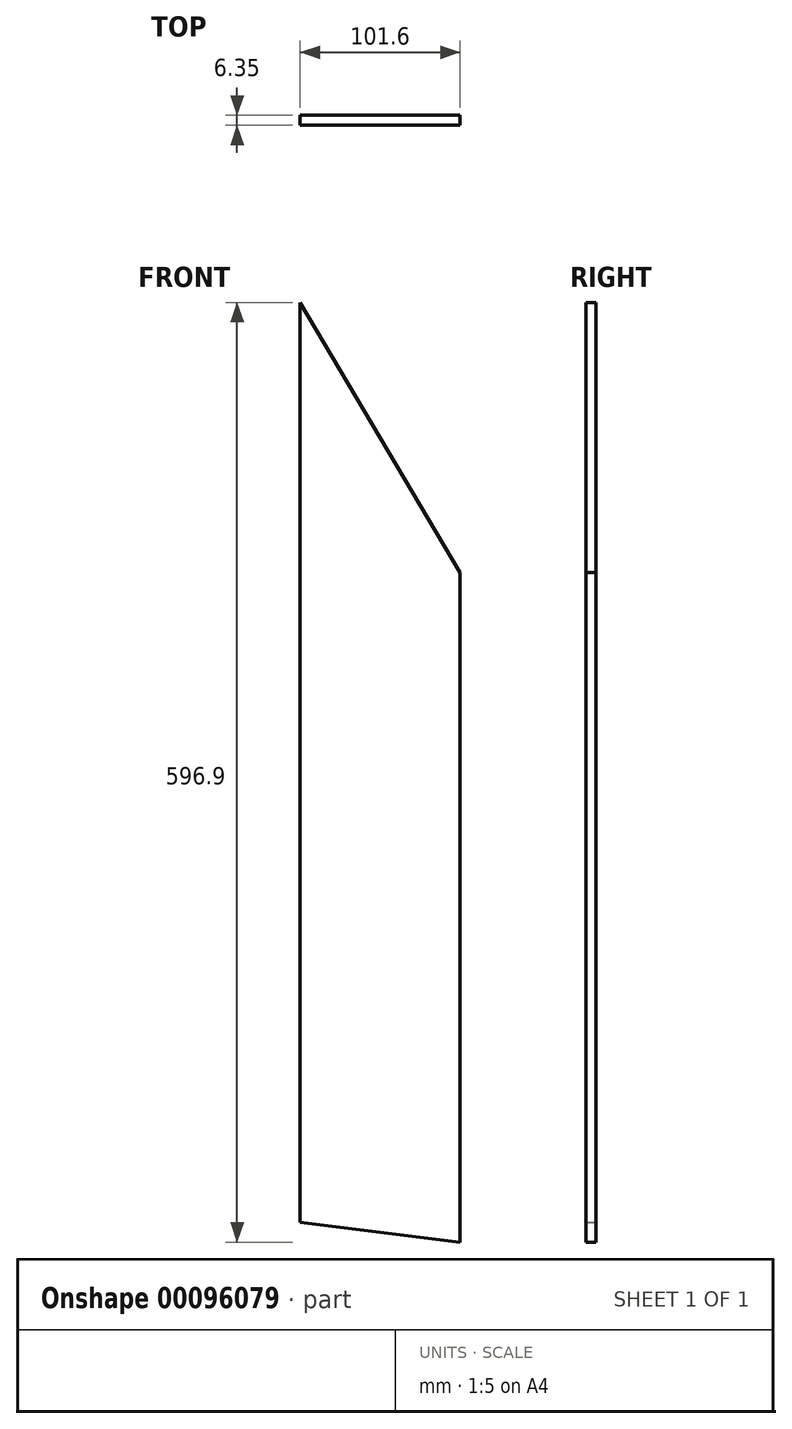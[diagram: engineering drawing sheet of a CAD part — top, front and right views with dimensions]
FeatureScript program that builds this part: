
annotation { "Feature Type Name" : "Feature", "Feature Type Description" : "" }
export const myFeature = defineFeature(function(context is Context, id is Id, definition is map)
    precondition{}
    {
        {
            var Q0;
            Q0=qCreatedBy(makeId("Front.planeOp"),FACE);
            var sketch = newSketch(context, id + "F0", { "sketchPlane" : qUnion([Q0])});
            skLineSegment(sketch, "E0", {"start": v(0, 371.58) * mm, "end": v(101.6, 200.13) * mm});
            skLineSegment(sketch, "E1", {"start": v(101.6, 200.13) * mm, "end": v(101.6, -225.32) * mm});
            skLineSegment(sketch, "E2", {"start": v(101.6, -225.32) * mm, "end": v(0, -212.62) * mm});
            skLineSegment(sketch, "E3", {"start": v(0, -212.62) * mm, "end": v(0, 371.58) * mm});
            skLineSegment(sketch, "E4", {"start": v(0, 53.17) * mm, "end": v(101.6, 53.17) * mm, "construction": true});
            skLineSegment(sketch, "E5", {"start": v(101.6, 371.58) * mm, "end": v(101.6, 200.13) * mm, "construction": true});
            skLineSegment(sketch, "E6", {"start": v(0, 371.58) * mm, "end": v(101.6, 371.58) * mm, "construction": true});
            skLineSegment(sketch, "E7", {"start": v(0, -212.62) * mm, "end": v(0, -225.32) * mm, "construction": true});
            skLineSegment(sketch, "E8", {"start": v(0, -225.32) * mm, "end": v(101.6, -225.32) * mm, "construction": true});
            skSolve(sketch);
        }
        {
            var Q0;
            Q0=makeQuery(id+"F0.imprint","IMPRINT",FACE,{"disambiguationData":[TD([[makeQuery(id+"F0.imprint","IMPRINT",EDGE,{"derivedFrom":sQuery(id+"F0.wireOp",EDGE,"E0")}),-1.0]])]});
            extrude(context, id + "F1", {"entities" : qUnion([Q0]), "depth" : 6.35 * mm});
        }
    });
